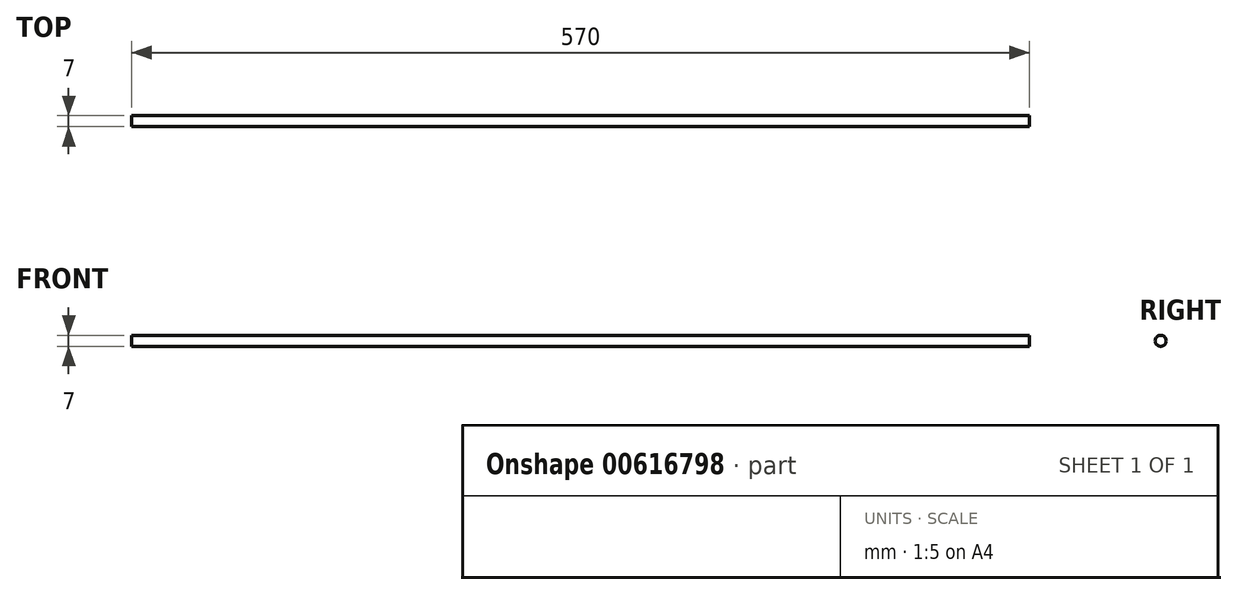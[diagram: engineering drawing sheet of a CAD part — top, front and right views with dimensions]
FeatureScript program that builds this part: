
annotation { "Feature Type Name" : "Feature", "Feature Type Description" : "" }
export const myFeature = defineFeature(function(context is Context, id is Id, definition is map)
    precondition{}
    {
        {
            var Q0;
            Q0=qCreatedBy(makeId("Right.planeOp"),FACE);
            var sketch = newSketch(context, id + "F0", { "sketchPlane" : qUnion([Q0])});
            skCircle(sketch, "E0", {"center": v(0, 0) * mm, "radius": 3.5 * mm});
            skSolve(sketch);
        }
        {
            var Q0;
            Q0=makeQuery(id+"F0.imprint","IMPRINT",FACE,{"disambiguationData":[TD([[makeQuery(id+"F0.imprint","IMPRINT",EDGE,{"derivedFrom":sQuery(id+"F0.wireOp",EDGE,"E0")}),1.0]])]});
            extrude(context, id + "F1", {"entities" : qUnion([Q0]), "depth" : 570 * mm, "offsetDistance" : 25 * mm, "symmetric" : true});
        }
    });
